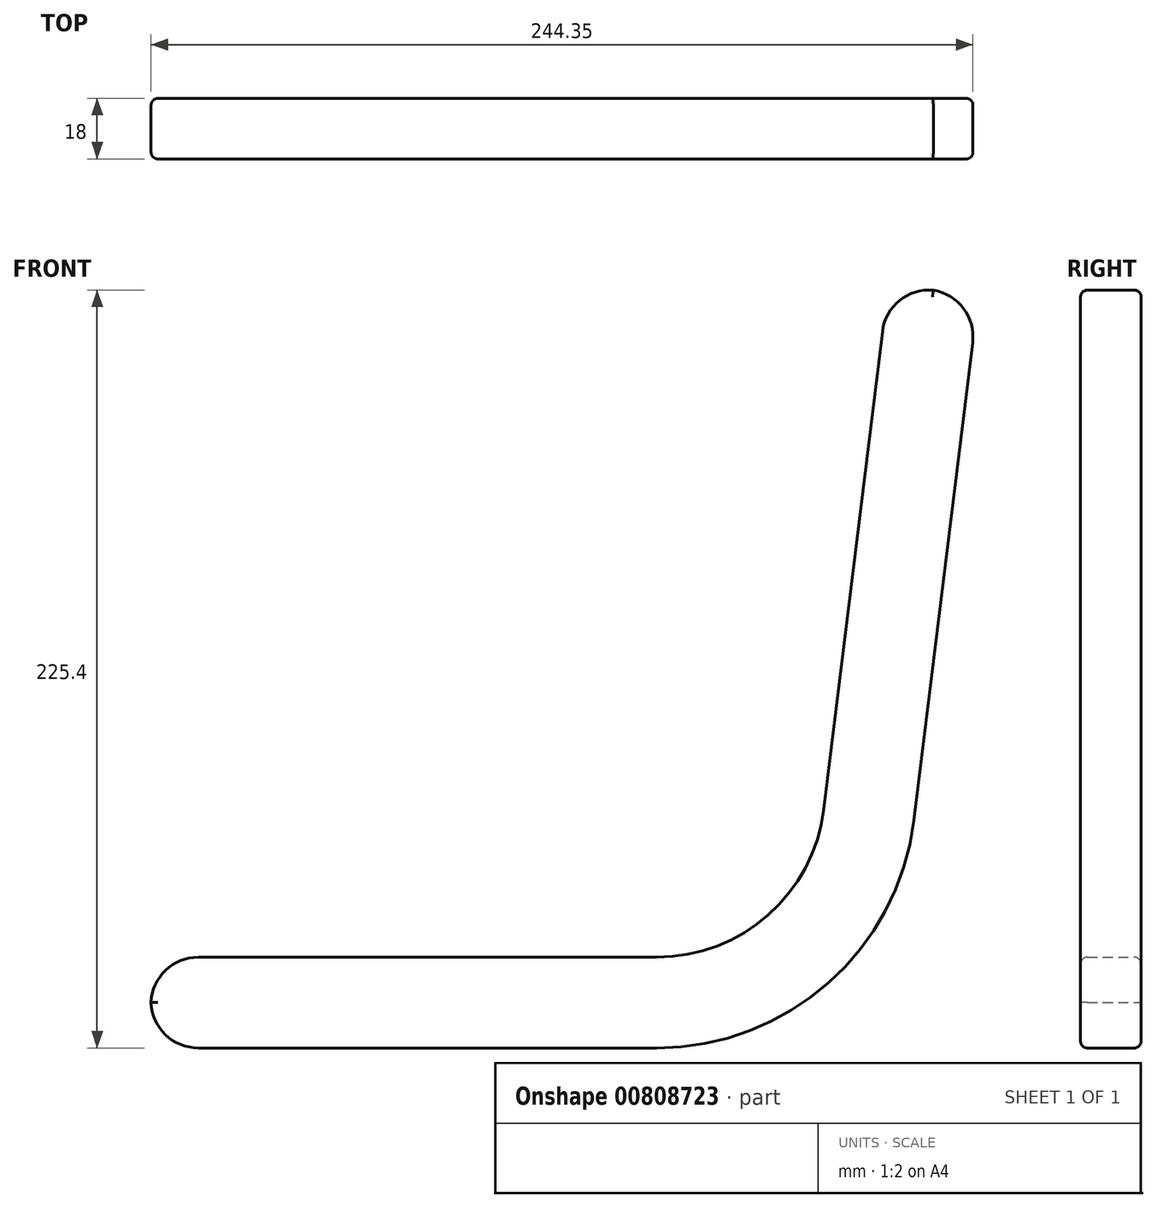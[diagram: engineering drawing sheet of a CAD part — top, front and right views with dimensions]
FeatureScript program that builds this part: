
annotation { "Feature Type Name" : "Feature", "Feature Type Description" : "" }
export const myFeature = defineFeature(function(context is Context, id is Id, definition is map)
    precondition{}
    {
        {
            var Q0;
            Q0=qCreatedBy(makeId("Front.planeOp"),FACE);
            var sketch = newSketch(context, id + "F0", { "sketchPlane" : qUnion([Q0])});
            skLineSegment(sketch, "E0", {"start": v(5.4, 43.9) * mm, "end": v(22.85, 186.1) * mm});
            skLineSegment(sketch, "E1", {"start": v(-44.24, 0) * mm, "end": v(-180.6, 0) * mm});
            skPoint(sketch, "E2.visualSharp", {"position": v(0, 0) * mm});
            skArc(sketch, "E2.filletArc", {"start": v(-44.24, 0) * mm, "mid": v(-11.1, 12.55) * mm, "end": v(5.4, 43.9) * mm});
            skLineSegment(sketch, "E3.0", {"start": v(32.19, 40.62) * mm, "end": v(49.65, 182.81) * mm});
            skArc(sketch, "E3.1", {"start": v(-44.24, -27) * mm, "mid": v(6.79, -7.67) * mm, "end": v(32.19, 40.62) * mm});
            skLineSegment(sketch, "E3.2", {"start": v(-44.24, -27) * mm, "end": v(-180.6, -27) * mm});
            skLineSegment(sketch, "E4", {"start": v(37.46, 198.42) * mm, "end": v(38.45, 198.3) * mm});
            skLineSegment(sketch, "E5", {"start": v(-194.6, -13) * mm, "end": v(-194.6, -14) * mm});
            skPoint(sketch, "E6.visualSharp", {"position": v(51.36, 196.7) * mm});
            skArc(sketch, "E6.filletArc", {"start": v(49.65, 182.81) * mm, "mid": v(46.79, 193.14) * mm, "end": v(37.46, 198.42) * mm});
            skPoint(sketch, "E7.visualSharp", {"position": v(-194.6, -27) * mm});
            skArc(sketch, "E7.filletArc", {"start": v(-194.6, -13) * mm, "mid": v(-190.5, -22.9) * mm, "end": v(-180.6, -27) * mm});
            skPoint(sketch, "E8.visualSharp", {"position": v(-194.6, 0) * mm});
            skArc(sketch, "E8.filletArc", {"start": v(-180.6, 0) * mm, "mid": v(-190.5, -4.1) * mm, "end": v(-194.6, -14) * mm});
            skPoint(sketch, "E9.visualSharp", {"position": v(24.56, 200) * mm});
            skArc(sketch, "E9.filletArc", {"start": v(38.45, 198.3) * mm, "mid": v(28.13, 195.43) * mm, "end": v(22.85, 186.1) * mm});
            skSolve(sketch);
        }
        {
            var Q0;
            {var subQ5=sQuery(id+"F0.wireOp",EDGE,"E0");Q0=makeQuery(id+"F0.imprint","IMPRINT",FACE,{"disambiguationData":[TD([[makeQuery(id+"F0.imprint","IMPRINT",EDGE,{"derivedFrom":subQ5}),-1.0]])]});}
            extrude(context, id + "F1", {"entities" : qUnion([Q0]), "depth" : 18 * mm, "offsetDistance" : 25 * mm});
        }
        {
            var Q0;
            Q0=makeQuery(id+"F1.opExtrude","CAP_FACE",FACE,{"disambiguationData":[OSD([sQuery(id+"F0.wireOp",EDGE,"E0"),sQuery(id+"F0.wireOp",EDGE,"E1"),sQuery(id+"F0.wireOp",EDGE,"E2.filletArc"),sQuery(id+"F0.wireOp",EDGE,"E3.0"),sQuery(id+"F0.wireOp",EDGE,"E3.1"),sQuery(id+"F0.wireOp",EDGE,"E3.2"),sQuery(id+"F0.wireOp",EDGE,"E6.filletArc"),sQuery(id+"F0.wireOp",EDGE,"E7.filletArc"),sQuery(id+"F0.wireOp",EDGE,"E8.filletArc"),sQuery(id+"F0.wireOp",EDGE,"E9.filletArc")])],"isStart":false});
            var Q1;
            Q1=makeQuery(id+"F1.opExtrude","CAP_FACE",FACE,{"disambiguationData":[OSD([sQuery(id+"F0.wireOp",EDGE,"E0"),sQuery(id+"F0.wireOp",EDGE,"E1"),sQuery(id+"F0.wireOp",EDGE,"E2.filletArc"),sQuery(id+"F0.wireOp",EDGE,"E3.0"),sQuery(id+"F0.wireOp",EDGE,"E3.1"),sQuery(id+"F0.wireOp",EDGE,"E3.2"),sQuery(id+"F0.wireOp",EDGE,"E6.filletArc"),sQuery(id+"F0.wireOp",EDGE,"E7.filletArc"),sQuery(id+"F0.wireOp",EDGE,"E8.filletArc"),sQuery(id+"F0.wireOp",EDGE,"E9.filletArc")])],"isStart":true});
            fillet(context, id + "F2", {"entities" : qUnion([Q0, Q1]), "radius" : 2 * mm, "tangentPropagation" : true, "allowEdgeOverflow" : false});
        }
        {
            var Q0;
            Q0=makeQuery(id+"F1.opExtrude","CAP_FACE",FACE,{"disambiguationData":[OSD([sQuery(id+"F0.wireOp",EDGE,"E0"),sQuery(id+"F0.wireOp",EDGE,"E1"),sQuery(id+"F0.wireOp",EDGE,"E2.filletArc"),sQuery(id+"F0.wireOp",EDGE,"E3.0"),sQuery(id+"F0.wireOp",EDGE,"E3.1"),sQuery(id+"F0.wireOp",EDGE,"E3.2"),sQuery(id+"F0.wireOp",EDGE,"E6.filletArc"),sQuery(id+"F0.wireOp",EDGE,"E7.filletArc"),sQuery(id+"F0.wireOp",EDGE,"E8.filletArc"),sQuery(id+"F0.wireOp",EDGE,"E9.filletArc")])],"isStart":false});
            var sketch = newSketch(context, id + "F3", { "sketchPlane" : qUnion([Q0])});
            skLineSegment(sketch, "E10", {"start": v(-192.6, -13.5) * mm, "end": v(-162.6, -13.5) * mm, "construction": true});
            skPoint(sketch, "E11", {"position": v(-162.44, -13.5) * mm});
            skPoint(sketch, "E12", {"position": v(-28.23, -13.5) * mm});
            skLineSegment(sketch, "E13", {"start": v(-162.6, -13.5) * mm, "end": v(-32.6, -13.5) * mm, "construction": true});
            skLineSegment(sketch, "E14", {"start": v(-32.6, -13.5) * mm, "end": v(19.37, -13.5) * mm, "construction": true});
            skLineSegment(sketch, "E15", {"start": v(37.71, 196.36) * mm, "end": v(34.06, 166.58) * mm, "construction": true});
            skLineSegment(sketch, "E16", {"start": v(34.06, 166.58) * mm, "end": v(18.21, 37.55) * mm, "construction": true});
            skSolve(sketch);
        }
        {
            var Q0;
            Q0=makeQuery(id+"F1.opExtrude","CAP_FACE",FACE,{"disambiguationData":[OSD([sQuery(id+"F0.wireOp",EDGE,"E0"),sQuery(id+"F0.wireOp",EDGE,"E1"),sQuery(id+"F0.wireOp",EDGE,"E2.filletArc"),sQuery(id+"F0.wireOp",EDGE,"E3.0"),sQuery(id+"F0.wireOp",EDGE,"E3.1"),sQuery(id+"F0.wireOp",EDGE,"E3.2"),sQuery(id+"F0.wireOp",EDGE,"E6.filletArc"),sQuery(id+"F0.wireOp",EDGE,"E7.filletArc"),sQuery(id+"F0.wireOp",EDGE,"E8.filletArc"),sQuery(id+"F0.wireOp",EDGE,"E9.filletArc")])],"isStart":true});
            var sketch = newSketch(context, id + "F4", { "sketchPlane" : qUnion([Q0])});
            skLineSegment(sketch, "E17.0", {"start": v(162.6, -13.5) * mm, "end": v(32.6, -13.5) * mm});
            skLineSegment(sketch, "E18.0", {"start": v(-34.06, 166.58) * mm, "end": v(-18.21, 37.55) * mm});
            skSolve(sketch);
        }
    });
